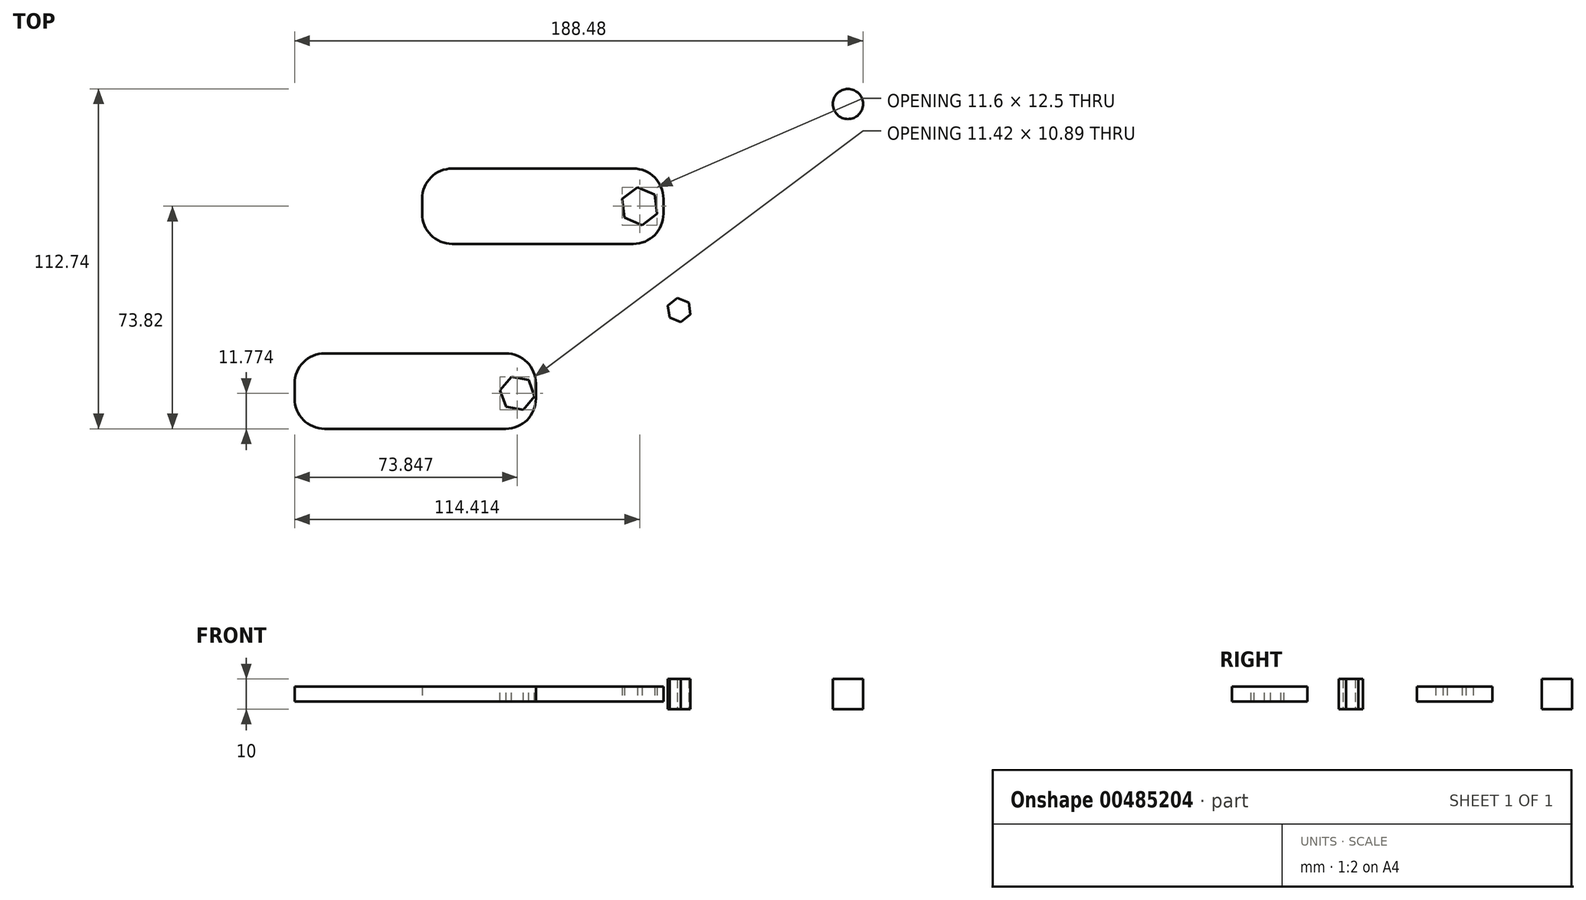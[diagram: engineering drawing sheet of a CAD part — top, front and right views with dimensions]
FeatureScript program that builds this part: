
annotation { "Feature Type Name" : "Feature", "Feature Type Description" : "" }
export const myFeature = defineFeature(function(context is Context, id is Id, definition is map)
    precondition{}
    {
        {
            var Q0;
            Q0=qCreatedBy(makeId("Top.planeOp"),FACE);
            var sketch = newSketch(context, id + "F0", { "sketchPlane" : qUnion([Q0])});
            skLineSegment(sketch, "E0.bottom", {"start": v(30, 12.5) * mm, "end": v(-30, 12.5) * mm});
            skLineSegment(sketch, "E0.top", {"start": v(30, -12.5) * mm, "end": v(-30, -12.5) * mm});
            skLineSegment(sketch, "E0.left", {"start": v(40, 2.5) * mm, "end": v(40, -2.5) * mm});
            skLineSegment(sketch, "E0.right", {"start": v(-40, 2.5) * mm, "end": v(-40, -2.5) * mm});
            skPoint(sketch, "E0.middle", {"position": v(0, 0) * mm});
            skPoint(sketch, "E1.visualSharp", {"position": v(-40, 12.5) * mm});
            skArc(sketch, "E1.filletArc", {"start": v(-30, 12.5) * mm, "mid": v(-37.07, 9.57) * mm, "end": v(-40, 2.5) * mm});
            skPoint(sketch, "E2.visualSharp", {"position": v(-40, -12.5) * mm});
            skArc(sketch, "E2.filletArc", {"start": v(-40, -2.5) * mm, "mid": v(-37.07, -9.57) * mm, "end": v(-30, -12.5) * mm});
            skPoint(sketch, "E3.visualSharp", {"position": v(40, 12.5) * mm});
            skArc(sketch, "E3.filletArc", {"start": v(40, 2.5) * mm, "mid": v(37.07, 9.57) * mm, "end": v(30, 12.5) * mm});
            skPoint(sketch, "E4.visualSharp", {"position": v(40, -12.5) * mm});
            skArc(sketch, "E4.filletArc", {"start": v(30, -12.5) * mm, "mid": v(37.07, -9.57) * mm, "end": v(40, -2.5) * mm});
            skSolve(sketch);
        }
        {
            var Q0;
            Q0 = qSketchRegion(id + "F0", true);
            extrude(context, id + "F1", {"entities" : qUnion([Q0]), "endBound" : BoundingType.SYMMETRIC, "depth" : 5 * mm});
        }
        {
            var Q0;
            Q0=makeQuery(id+"F1.opExtrude","CAP_FACE",FACE,{"disambiguationData":[OSD([sQuery(id+"F0.wireOp",EDGE,"E0.bottom"),sQuery(id+"F0.wireOp",EDGE,"E0.top"),sQuery(id+"F0.wireOp",EDGE,"E0.left"),sQuery(id+"F0.wireOp",EDGE,"E0.right"),sQuery(id+"F0.wireOp",EDGE,"E1.filletArc"),sQuery(id+"F0.wireOp",EDGE,"E2.filletArc"),sQuery(id+"F0.wireOp",EDGE,"E3.filletArc"),sQuery(id+"F0.wireOp",EDGE,"E4.filletArc")])],"isStart":true});
            var sketch = newSketch(context, id + "F2", { "sketchPlane" : qUnion([Q0])});
            skCircle(sketch, "E5.cCircle", {"center": v(32.12, 0) * mm, "radius": 5.45 * mm, "construction": true});
            skLineSegment(sketch, "E5.0", {"start": v(27.1, 3.8) * mm, "end": v(32.9, 6.25) * mm});
            skLineSegment(sketch, "E5.1", {"start": v(32.9, 6.25) * mm, "end": v(37.93, 2.45) * mm});
            skLineSegment(sketch, "E5.2", {"start": v(37.93, 2.45) * mm, "end": v(37.15, -3.8) * mm});
            skLineSegment(sketch, "E5.3", {"start": v(37.15, -3.8) * mm, "end": v(31.35, -6.25) * mm});
            skLineSegment(sketch, "E5.4", {"start": v(31.35, -6.25) * mm, "end": v(26.32, -2.45) * mm});
            skLineSegment(sketch, "E5.5", {"start": v(26.32, -2.45) * mm, "end": v(27.1, 3.8) * mm});
            skPoint(sketch, "E5.0.midPoint", {"position": v(30, 5.02) * mm});
            skCircle(sketch, "E6", {"center": v(32.12, 0) * mm, "radius": 3.56 * mm});
            skSolve(sketch);
        }
        {
            var Q0;
            Q0 = qSketchRegion(id + "F2", true);
            extrude(context, id + "F3", {"entities" : qUnion([Q0]), "operationType" : NewBodyOperationType.REMOVE, "oppositeDirection" : true, "depth" : 20 * mm});
        }
        {
            var Q0;
            Q0=makeQuery(id+"F3.boolean.opBoolean","SPLIT",FACE,{"disambiguationData":[TD([makeQuery(id+"F3.opExtrude","SWEPT_FACE",FACE,{"disambiguationData":[OSD([sQuery(id+"F2.wireOp",EDGE,"E6")])]})])],"derivedFrom":makeQuery(id+"F1.opExtrude","CAP_FACE",FACE,{"disambiguationData":[OSD([sQuery(id+"F0.wireOp",EDGE,"E0.bottom"),sQuery(id+"F0.wireOp",EDGE,"E0.top"),sQuery(id+"F0.wireOp",EDGE,"E0.left"),sQuery(id+"F0.wireOp",EDGE,"E0.right"),sQuery(id+"F0.wireOp",EDGE,"E1.filletArc"),sQuery(id+"F0.wireOp",EDGE,"E2.filletArc"),sQuery(id+"F0.wireOp",EDGE,"E3.filletArc"),sQuery(id+"F0.wireOp",EDGE,"E4.filletArc")])],"isStart":true})});
            extrude(context, id + "F4", {"entities" : qUnion([Q0]), "operationType" : NewBodyOperationType.REMOVE, "oppositeDirection" : true, "depth" : 20 * mm});
        }
        {
            var Q0;
            Q0=qCreatedBy(makeId("Top.planeOp"),FACE);
            var sketch = newSketch(context, id + "F5", { "sketchPlane" : qUnion([Q0])});
            skLineSegment(sketch, "E7.bottom", {"start": v(-72.3, -73.82) * mm, "end": v(-12.3, -73.82) * mm});
            skLineSegment(sketch, "E7.top", {"start": v(-72.3, -48.82) * mm, "end": v(-12.3, -48.82) * mm});
            skLineSegment(sketch, "E7.left", {"start": v(-82.3, -63.82) * mm, "end": v(-82.3, -58.82) * mm});
            skLineSegment(sketch, "E7.right", {"start": v(-2.3, -63.82) * mm, "end": v(-2.3, -58.82) * mm});
            skPoint(sketch, "E8.visualSharp", {"position": v(-82.3, -73.82) * mm});
            skArc(sketch, "E8.filletArc", {"start": v(-82.3, -63.82) * mm, "mid": v(-79.36, -70.9) * mm, "end": v(-72.3, -73.82) * mm});
            skPoint(sketch, "E9.visualSharp", {"position": v(-82.3, -48.82) * mm});
            skArc(sketch, "E9.filletArc", {"start": v(-72.3, -48.82) * mm, "mid": v(-79.36, -51.75) * mm, "end": v(-82.3, -58.82) * mm});
            skPoint(sketch, "E10.visualSharp", {"position": v(-2.3, -73.82) * mm});
            skArc(sketch, "E10.filletArc", {"start": v(-12.3, -73.82) * mm, "mid": v(-5.22, -70.9) * mm, "end": v(-2.3, -63.82) * mm});
            skPoint(sketch, "E11.visualSharp", {"position": v(-2.3, -48.82) * mm});
            skArc(sketch, "E11.filletArc", {"start": v(-2.3, -58.82) * mm, "mid": v(-5.22, -51.75) * mm, "end": v(-12.3, -48.82) * mm});
            skSolve(sketch);
        }
        {
            var Q0;
            Q0 = qSketchRegion(id + "F5", true);
            extrude(context, id + "F6", {"entities" : qUnion([Q0]), "endBound" : BoundingType.SYMMETRIC, "depth" : 5 * mm});
        }
        {
            var Q0;
            Q0=makeQuery(id+"F6.opExtrude","CAP_FACE",FACE,{"disambiguationData":[OSD([sQuery(id+"F5.wireOp",EDGE,"E7.bottom"),sQuery(id+"F5.wireOp",EDGE,"E7.top"),sQuery(id+"F5.wireOp",EDGE,"E7.left"),sQuery(id+"F5.wireOp",EDGE,"E7.right"),sQuery(id+"F5.wireOp",EDGE,"E8.filletArc"),sQuery(id+"F5.wireOp",EDGE,"E9.filletArc"),sQuery(id+"F5.wireOp",EDGE,"E10.filletArc"),sQuery(id+"F5.wireOp",EDGE,"E11.filletArc")])],"isStart":false});
            var sketch = newSketch(context, id + "F7", { "sketchPlane" : qUnion([Q0])});
            skCircle(sketch, "E12.cCircle", {"center": v(-8.44, -62.05) * mm, "radius": 5.02 * mm, "construction": true});
            skLineSegment(sketch, "E12.0", {"start": v(-14.15, -61.04) * mm, "end": v(-10.43, -56.6) * mm});
            skLineSegment(sketch, "E12.1", {"start": v(-10.43, -56.6) * mm, "end": v(-4.72, -57.6) * mm});
            skLineSegment(sketch, "E12.2", {"start": v(-4.72, -57.6) * mm, "end": v(-2.73, -63.05) * mm});
            skLineSegment(sketch, "E12.3", {"start": v(-2.73, -63.05) * mm, "end": v(-6.46, -67.5) * mm});
            skLineSegment(sketch, "E12.4", {"start": v(-6.46, -67.5) * mm, "end": v(-12.17, -66.49) * mm});
            skLineSegment(sketch, "E12.5", {"start": v(-12.17, -66.49) * mm, "end": v(-14.15, -61.04) * mm});
            skPoint(sketch, "E12.0.midPoint", {"position": v(-12.3, -58.82) * mm});
            skSolve(sketch);
        }
        {
            var Q0;
            Q0 = qSketchRegion(id + "F7", true);
            extrude(context, id + "F8", {"entities" : qUnion([Q0]), "operationType" : NewBodyOperationType.REMOVE, "oppositeDirection" : true, "depth" : 6 * mm});
        }
        {
            var Q0;
            Q0=qCreatedBy(makeId("Top.planeOp"),FACE);
            var sketch = newSketch(context, id + "F9", { "sketchPlane" : qUnion([Q0])});
            skCircle(sketch, "E13", {"center": v(101.19, 33.92) * mm, "radius": 5 * mm});
            skPoint(sketch, "E13.first.point", {"position": v(97.34, 37.12) * mm});
            skPoint(sketch, "E13.second.point", {"position": v(106.13, 33.15) * mm});
            skPoint(sketch, "E13.third.point", {"position": v(103.18, 38.5) * mm});
            skSolve(sketch);
        }
        {
            var Q0;
            Q0 = qSketchRegion(id + "F9", true);
            extrude(context, id + "F10", {"entities" : qUnion([Q0]), "endBound" : BoundingType.SYMMETRIC, "depth" : 10 * mm});
        }
        {
            var Q0;
            Q0=qCreatedBy(makeId("Top.planeOp"),FACE);
            var sketch = newSketch(context, id + "F11", { "sketchPlane" : qUnion([Q0])});
            skCircle(sketch, "E14.cCircle", {"center": v(45.22, -34.44) * mm, "radius": 3.5 * mm, "construction": true});
            skLineSegment(sketch, "E14.0", {"start": v(45.8, -38.44) * mm, "end": v(42.05, -36.94) * mm});
            skLineSegment(sketch, "E14.1", {"start": v(42.05, -36.94) * mm, "end": v(41.47, -32.94) * mm});
            skLineSegment(sketch, "E14.2", {"start": v(41.47, -32.94) * mm, "end": v(44.64, -30.44) * mm});
            skLineSegment(sketch, "E14.3", {"start": v(44.64, -30.44) * mm, "end": v(48.4, -31.94) * mm});
            skLineSegment(sketch, "E14.4", {"start": v(48.4, -31.94) * mm, "end": v(48.97, -35.94) * mm});
            skLineSegment(sketch, "E14.5", {"start": v(48.97, -35.94) * mm, "end": v(45.8, -38.44) * mm});
            skPoint(sketch, "E14.0.midPoint", {"position": v(43.92, -37.69) * mm});
            skSolve(sketch);
        }
        {
            var Q0;
            Q0 = qSketchRegion(id + "F11", true);
            extrude(context, id + "F12", {"entities" : qUnion([Q0]), "endBound" : BoundingType.SYMMETRIC, "depth" : 10 * mm});
        }
    });
